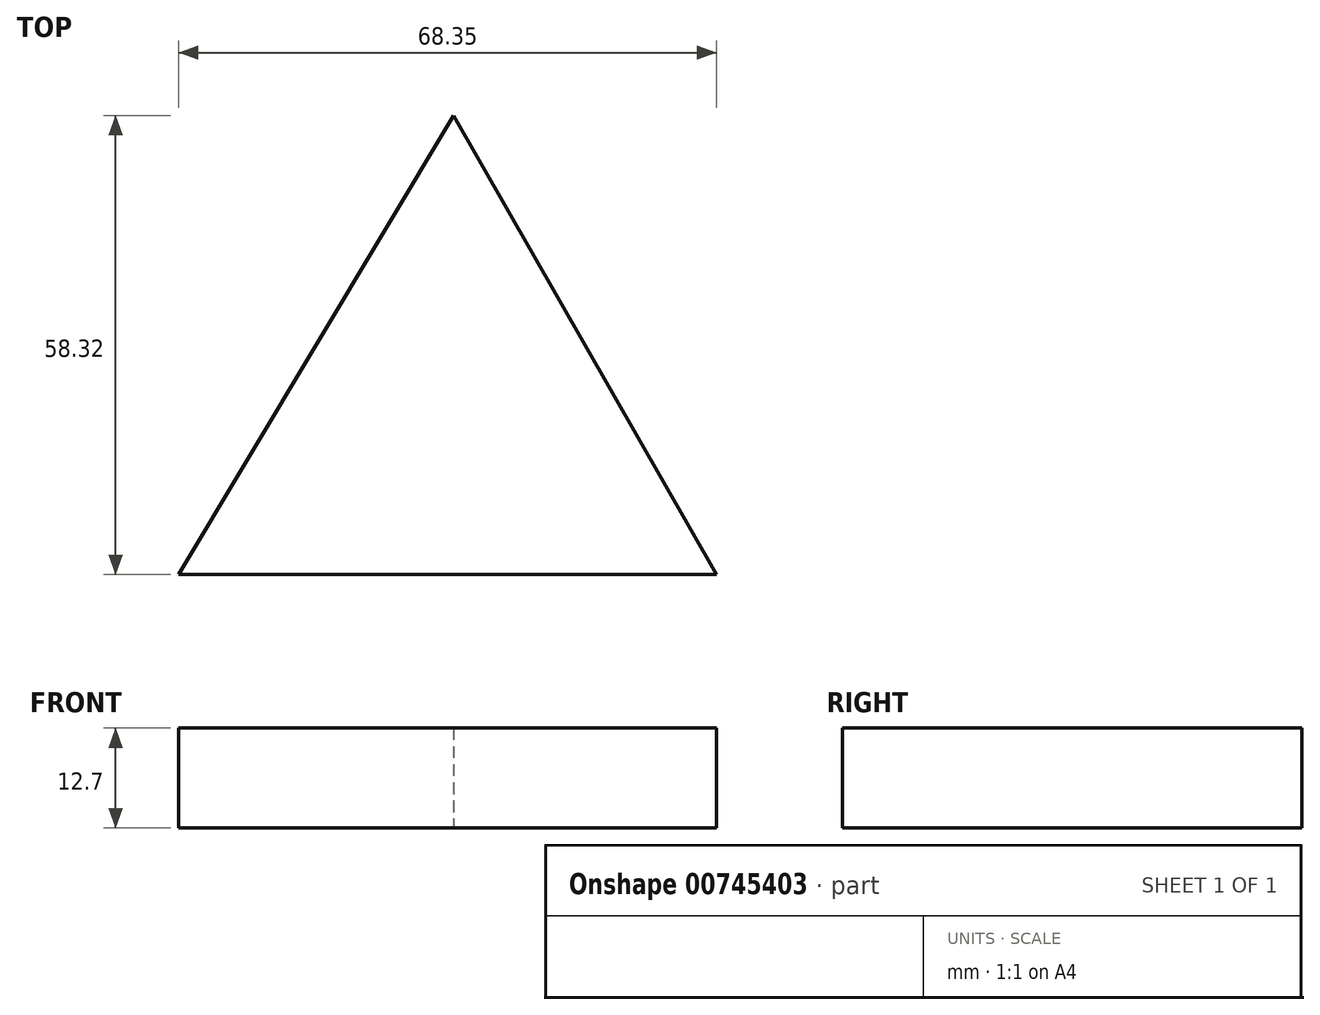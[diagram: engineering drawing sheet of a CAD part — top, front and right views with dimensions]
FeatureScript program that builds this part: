
annotation { "Feature Type Name" : "Feature", "Feature Type Description" : "" }
export const myFeature = defineFeature(function(context is Context, id is Id, definition is map)
    precondition{}
    {
        {
            var Q0;
            Q0=qCreatedBy(makeId("Top.planeOp"),FACE);
            var sketch = newSketch(context, id + "F0", { "sketchPlane" : qUnion([Q0])});
            skSolve(sketch);
        }
        {
            var Q0;
            Q0=qCreatedBy(makeId("Top.planeOp"),FACE);
            var sketch = newSketch(context, id + "F1", { "sketchPlane" : qUnion([Q0])});
            skLineSegment(sketch, "E0", {"start": v(-16.44, 15.5) * mm, "end": v(-51.37, -42.83) * mm});
            skLineSegment(sketch, "E1", {"start": v(-16.44, 15.5) * mm, "end": v(16.98, -42.83) * mm});
            skLineSegment(sketch, "E2", {"start": v(-51.37, -42.83) * mm, "end": v(16.98, -42.83) * mm});
            skSolve(sketch);
        }
        {
            var Q0;
            Q0 = qSketchRegion(id + "F0", true);
            var Q1;
            Q1=makeQuery(id+"F1.imprint","IMPRINT",FACE,{"disambiguationData":[TD([[makeQuery(id+"F1.imprint","IMPRINT",EDGE,{"derivedFrom":sQuery(id+"F1.wireOp",EDGE,"E0")}),1.0]])]});
            extrude(context, id + "F2", {"entities" : qUnion([Q0, Q1]), "depth" : 12.7 * mm, "offsetDistance" : 25.4 * mm});
        }
    });
